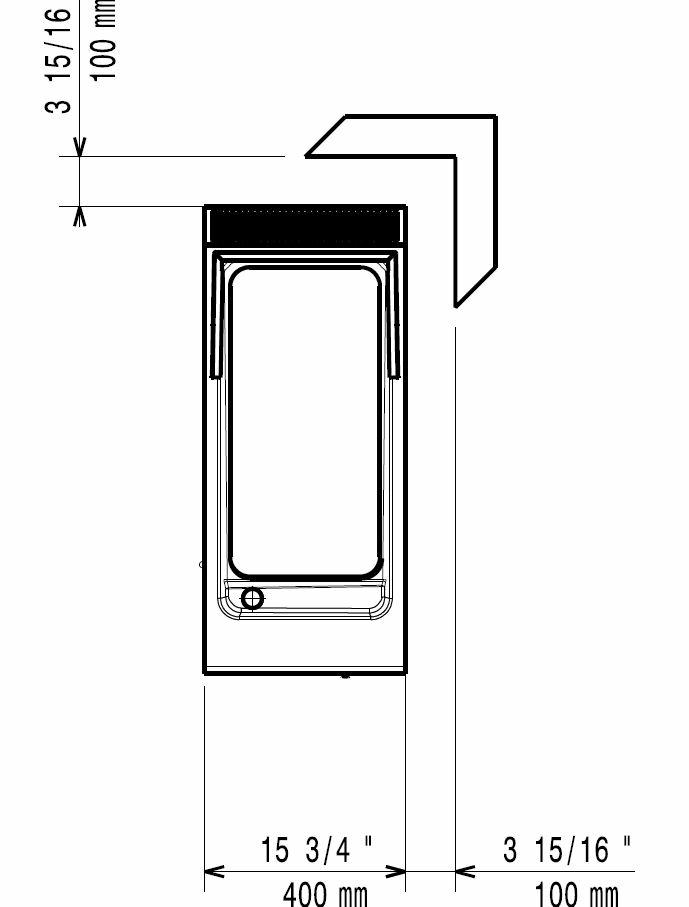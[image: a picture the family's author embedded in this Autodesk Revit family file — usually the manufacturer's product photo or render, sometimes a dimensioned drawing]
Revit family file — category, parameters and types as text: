
# Revit family: QF_ELECTROLUXPROFESSIONAL_391402_E9IINAAOMCA
name_source: partatom
category: Specialty Equipment
revit_build: Autodesk Revit 2018 (Build: 20190510_1515(x64)
units: mm (PartAtom-declared; Revit-internal decimal feet)

## family parameters
Always vertical = Yes
Cut with Voids When Loaded = No
Part Type = Normal
Room Calculation Point = No
Round Connector Dimension = Use Diameter
Shared = No
Work Plane-Based = No

## types (1)
- QF_ELECTROLUXPROFESSIONAL_391402_E9IINAAOMCA
    Depth = 930 mm  [stored 3.05118 ft]
    Description = 900XP HALF MODULE GAS FRY TOP, SMOOTH HORIZONTAL PLATE, MILD STEEL
    Direct Waste Size = 0"
    Gas Connection Height = 0 mm  [stored 0 ft]
    Gas Size = 1"
    HP = 0 HP
    Height = 410 mm
    Manufacturer = ELECTROLUX
    Model = 391048
    URL = www.electrolux.com/foodservice
    URL Cutsheet = www.electrolux.com/foodservice
    Watts = 0 W
    Weight in Pounds = 55
    Width = 400 mm  [stored 1.31234 ft]

note: [stored X ft] marks values corroborated as IEEE doubles in the binary element streams (Revit-internal decimal feet)

## geometry (parser evidence)
native form markers: Blend x28, Sweep x2
no freeform markers — native parametric forms only
